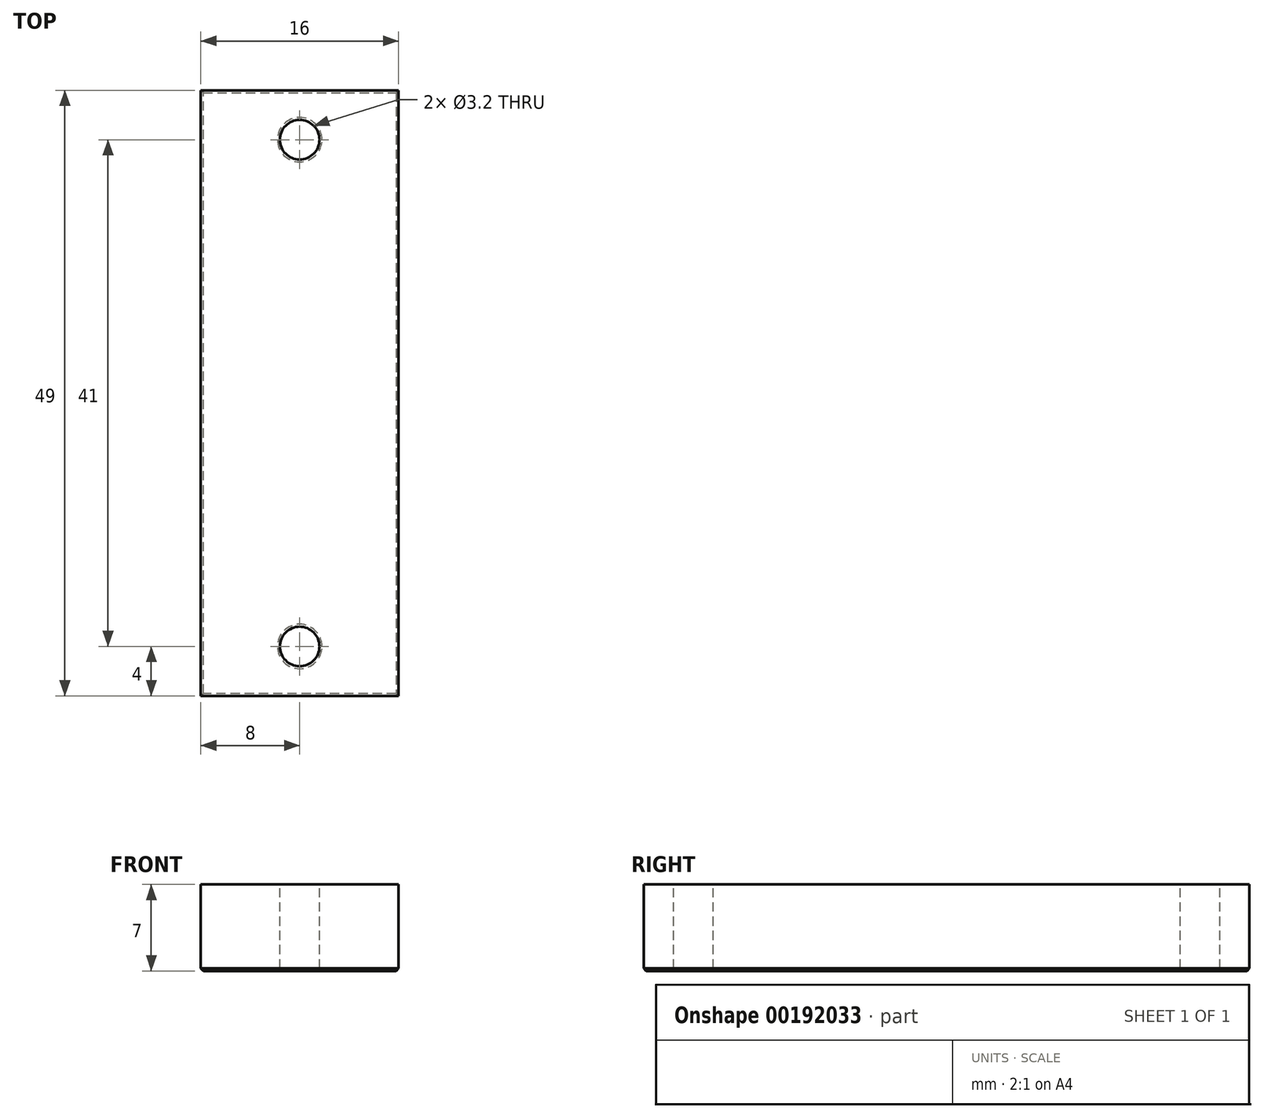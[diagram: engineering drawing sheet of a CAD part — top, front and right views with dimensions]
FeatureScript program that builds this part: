
annotation { "Feature Type Name" : "Feature", "Feature Type Description" : "" }
export const myFeature = defineFeature(function(context is Context, id is Id, definition is map)
    precondition{}
    {
        {
            var Q0;
            Q0=qCreatedBy(makeId("Top.planeOp"),FACE);
            var sketch = newSketch(context, id + "F0", { "sketchPlane" : qUnion([Q0])});
            skLineSegment(sketch, "E0.bottom", {"start": v(8, 24.5) * mm, "end": v(-8, 24.5) * mm});
            skLineSegment(sketch, "E0.top", {"start": v(8, -24.5) * mm, "end": v(-8, -24.5) * mm});
            skLineSegment(sketch, "E0.left", {"start": v(8, 24.5) * mm, "end": v(8, -24.5) * mm});
            skLineSegment(sketch, "E0.right", {"start": v(-8, 24.5) * mm, "end": v(-8, -24.5) * mm});
            skPoint(sketch, "E0.middle", {"position": v(0, 0) * mm});
            skLineSegment(sketch, "E1", {"start": v(0, 20.5) * mm, "end": v(0, -20.5) * mm, "construction": true});
            skCircle(sketch, "E2", {"center": v(0, 20.5) * mm, "radius": 1.6 * mm});
            skCircle(sketch, "E3", {"center": v(0, -20.5) * mm, "radius": 1.6 * mm});
            skSolve(sketch);
        }
        {
            var Q0;
            Q0=qCreatedBy(makeId("Front.planeOp"),FACE);
            var sketch = newSketch(context, id + "F1", { "sketchPlane" : qUnion([Q0])});
            skLineSegment(sketch, "E4", {"start": v(0, 0) * mm, "end": v(0, 7) * mm});
            skSolve(sketch);
        }
        {
            var Q0;
            Q0 = qSketchRegion(id + "F0", true);
            var Q1;
            Q1=sQuery(id+"F1.wireOp",EDGE,"E4");
            sweep(context, id + "F2", {"profiles" : qUnion([Q0]), "path" : qUnion([Q1])});
        }
        {
            var Q0;
            Q0=makeQuery(id+"F2.opSweep","CAP_FACE",FACE,{"disambiguationData":[OSD([sQuery(id+"F0.wireOp",EDGE,"E0.bottom"),sQuery(id+"F0.wireOp",EDGE,"E0.top"),sQuery(id+"F0.wireOp",EDGE,"E0.left"),sQuery(id+"F0.wireOp",EDGE,"E0.right"),sQuery(id+"F0.wireOp",EDGE,"E2"),sQuery(id+"F0.wireOp",EDGE,"E3"),sQuery(id+"F1.wireOp",VERTEX,"E4.start")])],"isStart":true});
            chamfer(context, id + "F3", {"entities" : qUnion([Q0]), "width" : 0.2 * mm});
        }
    });
